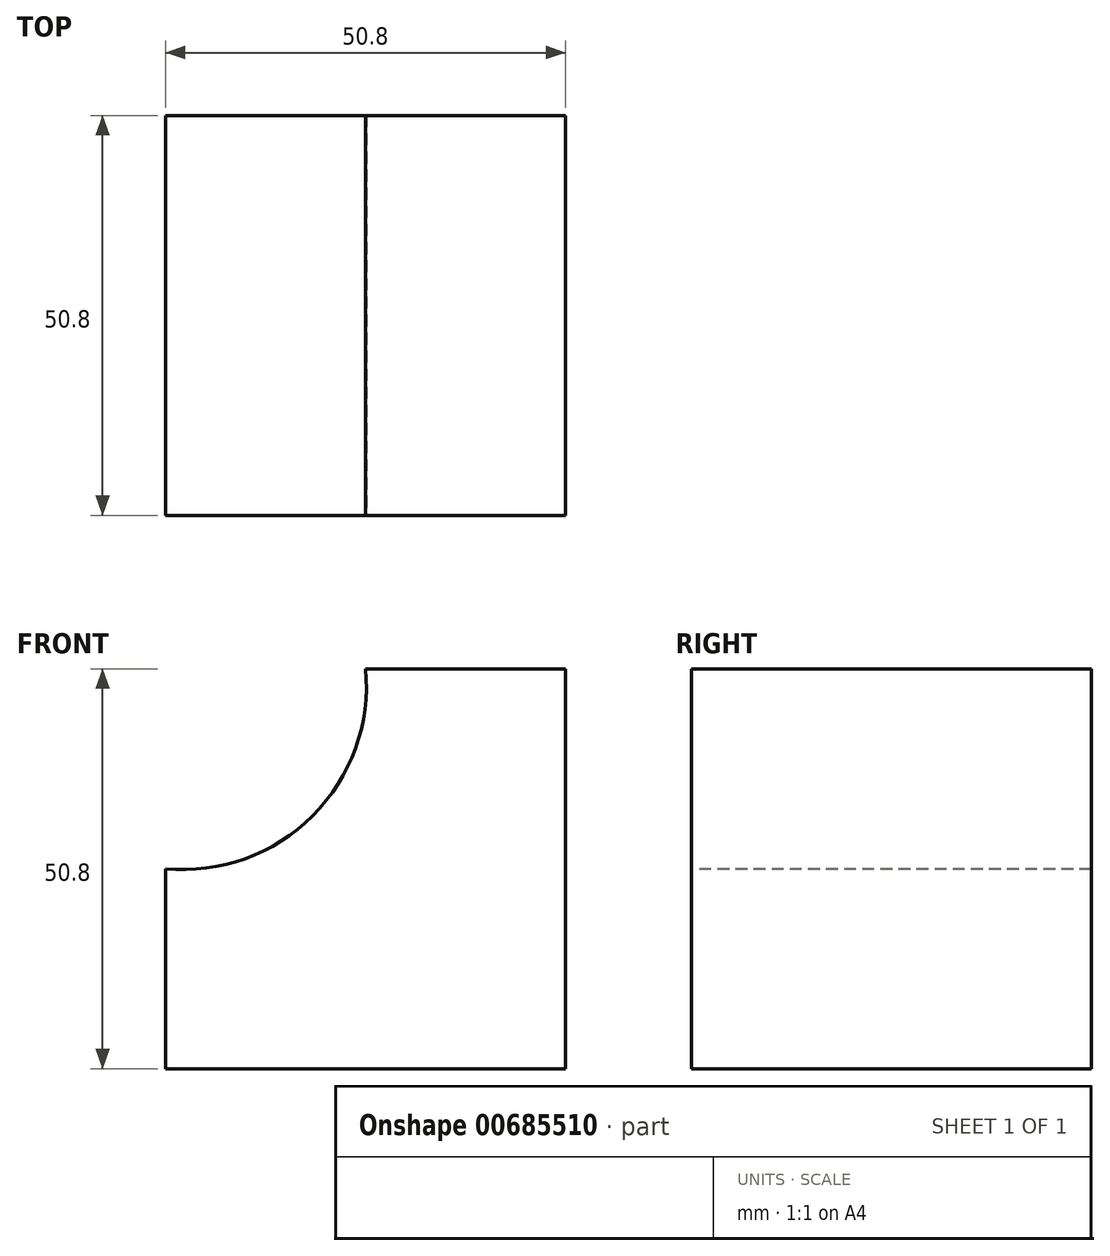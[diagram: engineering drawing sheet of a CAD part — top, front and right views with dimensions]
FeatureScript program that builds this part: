
annotation { "Feature Type Name" : "Feature", "Feature Type Description" : "" }
export const myFeature = defineFeature(function(context is Context, id is Id, definition is map)
    precondition{}
    {
        {
            var Q0;
            Q0=qCreatedBy(makeId("Front.planeOp"),FACE);
            var sketch = newSketch(context, id + "F0", { "sketchPlane" : qUnion([Q0])});
            skLineSegment(sketch, "E0.bottom", {"start": v(0, 0) * mm, "end": v(50.8, 0) * mm});
            skLineSegment(sketch, "E0.top", {"start": v(0, 50.8) * mm, "end": v(50.8, 50.8) * mm});
            skLineSegment(sketch, "E0.left", {"start": v(0, 0) * mm, "end": v(0, 50.8) * mm});
            skLineSegment(sketch, "E0.right", {"start": v(50.8, 0) * mm, "end": v(50.8, 50.8) * mm});
            skSolve(sketch);
        }
        {
            var Q0;
            Q0 = qSketchRegion(id + "F0", true);
            extrude(context, id + "F1", {"entities" : qUnion([Q0]), "depth" : 50.8 * mm, "offsetDistance" : 25.4 * mm});
        }
        {
            var Q0;
            Q0=makeQuery(id+"F1.opExtrude","CAP_FACE",FACE,{"disambiguationData":[OSD([sQuery(id+"F0.wireOp",EDGE,"E0.bottom"),sQuery(id+"F0.wireOp",EDGE,"E0.top"),sQuery(id+"F0.wireOp",EDGE,"E0.left"),sQuery(id+"F0.wireOp",EDGE,"E0.right")])],"isStart":false});
            var sketch = newSketch(context, id + "F2", { "sketchPlane" : qUnion([Q0])});
            skArc(sketch, "E1", {"start": v(0, 25.4) * mm, "mid": v(18.68, 32.12) * mm, "end": v(25.4, 50.8) * mm});
            skSolve(sketch);
        }
        {
            var Q0;
            {var subQ0=sQuery(id+"F2.wireOp",EDGE,"E1");Q0=makeQuery(id+"F2.imprint","IMPRINT",FACE,{"disambiguationData":[TD([[makeQuery(id+"F2.imprint","IMPRINT",EDGE,{"derivedFrom":subQ0}),1.0]])]});}
            var sketch = newSketch(context, id + "F3", { "sketchPlane" : qUnion([Q0])});
            skSolve(sketch);
        }
        {
            var Q0;
            Q0 = qSketchRegion(id + "F3", true);
            var Q1;
            {var subQ0=sQuery(id+"F2.wireOp",EDGE,"E1");Q1=makeQuery(id+"F2.imprint","IMPRINT",FACE,{"disambiguationData":[TD([[makeQuery(id+"F2.imprint","IMPRINT",EDGE,{"derivedFrom":subQ0}),1.0]])]});}
            extrude(context, id + "F4", {"entities" : qUnion([Q0, Q1]), "operationType" : NewBodyOperationType.REMOVE, "oppositeDirection" : true, "depth" : 50.8 * mm, "offsetDistance" : 25.4 * mm});
        }
    });
